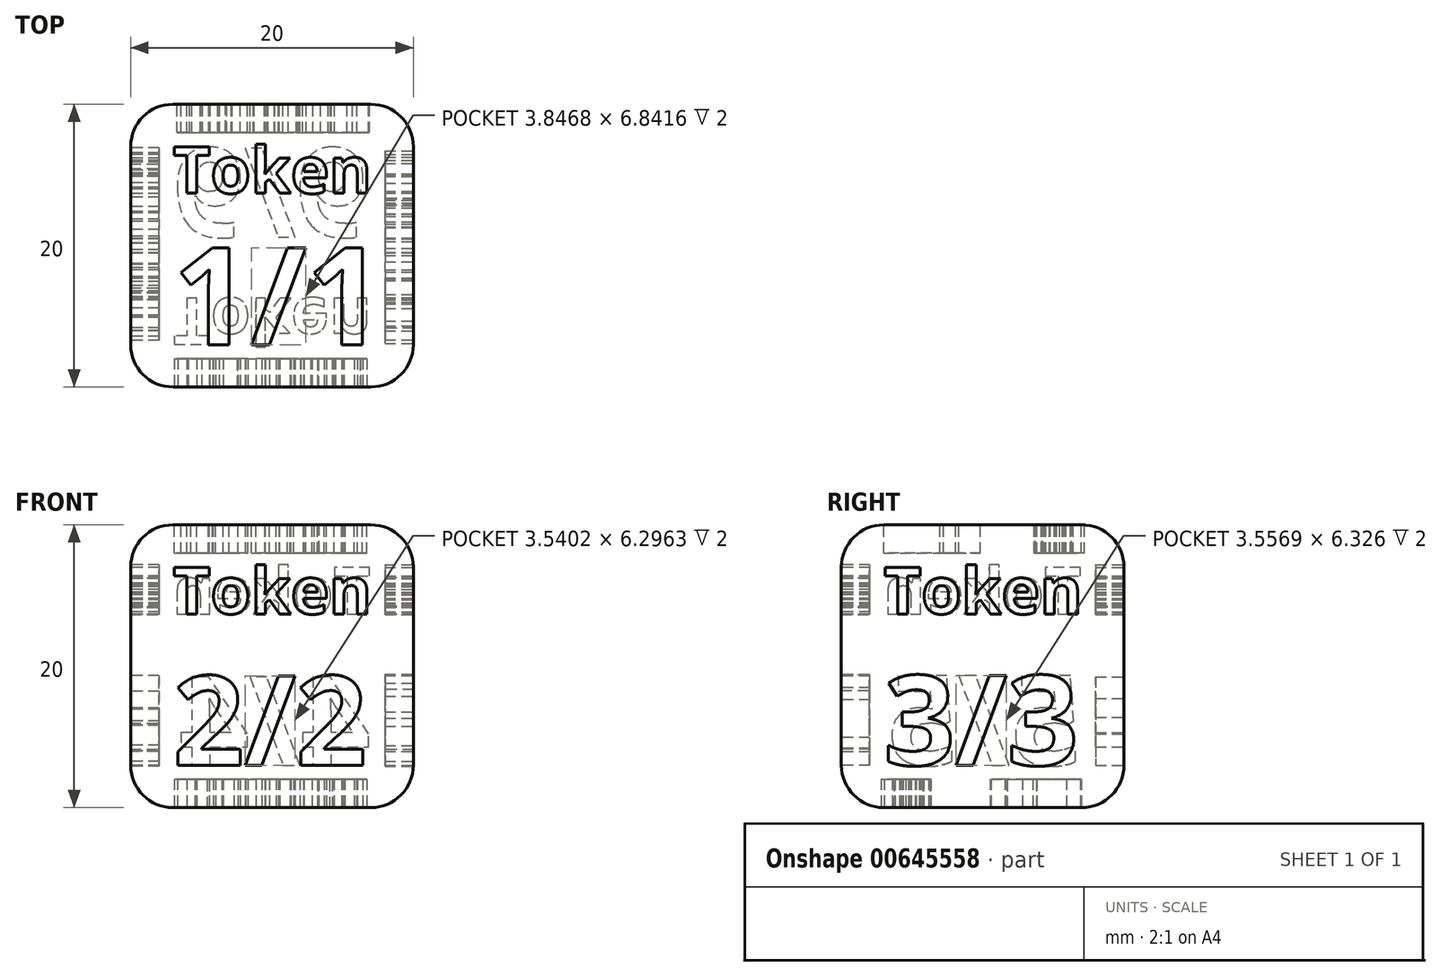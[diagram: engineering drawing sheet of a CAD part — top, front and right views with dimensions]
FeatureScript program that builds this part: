
annotation { "Feature Type Name" : "Feature", "Feature Type Description" : "" }
export const myFeature = defineFeature(function(context is Context, id is Id, definition is map)
    precondition{}
    {
        {
            var Q0;
            Q0=qCreatedBy(makeId("Top.planeOp"),FACE);
            var sketch = newSketch(context, id + "F0", { "sketchPlane" : qUnion([Q0])});
            skLineSegment(sketch, "E0.bottom", {"start": v(0, 0) * mm, "end": v(20, 0) * mm});
            skLineSegment(sketch, "E0.top", {"start": v(0, 20) * mm, "end": v(20, 20) * mm});
            skLineSegment(sketch, "E0.left", {"start": v(0, 0) * mm, "end": v(0, 20) * mm});
            skLineSegment(sketch, "E0.right", {"start": v(20, 0) * mm, "end": v(20, 20) * mm});
            skSolve(sketch);
        }
        {
            var Q0;
            Q0 = qSketchRegion(id + "F0", true);
            extrude(context, id + "F1", {"entities" : qUnion([Q0]), "depth" : 20 * mm, "offsetDistance" : 25 * mm});
        }
        {
            var Q0;
            Q0=makeQuery(id+"F1.opExtrude","CAP_EDGE",EDGE,{"disambiguationData":[OSD([sQuery(id+"F0.wireOp",EDGE,"E0.top")])],"isStart":true});
            var Q1;
            Q1=makeQuery(id+"F1.opExtrude","CAP_EDGE",EDGE,{"disambiguationData":[OSD([sQuery(id+"F0.wireOp",EDGE,"E0.left")])],"isStart":true});
            var Q2;
            Q2=makeQuery(id+"F1.opExtrude","SWEPT_EDGE",EDGE,{"disambiguationData":[OSD([sQuery(id+"F0.wireOp",EDGE,"E0.top"),sQuery(id+"F0.wireOp",EDGE,"E0.left")])]});
            var Q3;
            Q3=makeQuery(id+"F1.opExtrude","SWEPT_EDGE",EDGE,{"disambiguationData":[OSD([sQuery(id+"F0.wireOp",EDGE,"E0.top"),sQuery(id+"F0.wireOp",EDGE,"E0.right")])]});
            var Q4;
            Q4=makeQuery(id+"F1.opExtrude","CAP_EDGE",EDGE,{"disambiguationData":[OSD([sQuery(id+"F0.wireOp",EDGE,"E0.top")])],"isStart":false});
            var Q5;
            Q5=makeQuery(id+"F1.opExtrude","CAP_EDGE",EDGE,{"disambiguationData":[OSD([sQuery(id+"F0.wireOp",EDGE,"E0.right")])],"isStart":false});
            var Q6;
            Q6=makeQuery(id+"F1.opExtrude","CAP_EDGE",EDGE,{"disambiguationData":[OSD([sQuery(id+"F0.wireOp",EDGE,"E0.left")])],"isStart":false});
            var Q7;
            Q7=makeQuery(id+"F1.opExtrude","SWEPT_EDGE",EDGE,{"disambiguationData":[OSD([sQuery(id+"F0.wireOp",EDGE,"E0.bottom"),sQuery(id+"F0.wireOp",EDGE,"E0.left")])]});
            var Q8;
            Q8=makeQuery(id+"F1.opExtrude","CAP_EDGE",EDGE,{"disambiguationData":[OSD([sQuery(id+"F0.wireOp",EDGE,"E0.bottom")])],"isStart":false});
            var Q9;
            Q9=makeQuery(id+"F1.opExtrude","SWEPT_EDGE",EDGE,{"disambiguationData":[OSD([sQuery(id+"F0.wireOp",EDGE,"E0.bottom"),sQuery(id+"F0.wireOp",EDGE,"E0.right")])]});
            var Q10;
            Q10=makeQuery(id+"F1.opExtrude","CAP_EDGE",EDGE,{"disambiguationData":[OSD([sQuery(id+"F0.wireOp",EDGE,"E0.right")])],"isStart":true});
            var Q11;
            Q11=makeQuery(id+"F1.opExtrude","CAP_EDGE",EDGE,{"disambiguationData":[OSD([sQuery(id+"F0.wireOp",EDGE,"E0.bottom")])],"isStart":true});
            fillet(context, id + "F2", {"entities" : qUnion([Q0, Q1, Q2, Q3, Q4, Q5, Q6, Q7, Q8, Q9, Q10, Q11]), "radius" : 3 * mm, "tangentPropagation" : true, "allowEdgeOverflow" : false});
        }
        {
            var Q0;
            Q0=makeQuery(id+"F1.opExtrude","CAP_FACE",FACE,{"disambiguationData":[OSD([sQuery(id+"F0.wireOp",EDGE,"E0.bottom"),sQuery(id+"F0.wireOp",EDGE,"E0.top"),sQuery(id+"F0.wireOp",EDGE,"E0.left"),sQuery(id+"F0.wireOp",EDGE,"E0.right")])],"isStart":false});
            var sketch = newSketch(context, id + "F3", { "sketchPlane" : qUnion([Q0])});
            skText(sketch, "E1", { "text": "Token", "fontName": "OpenSans-Bold.ttf"});
            skText(sketch, "E2", { "text": "1/1", "fontName": "OpenSans-Bold.ttf"});
            const initialGuessF3  = {"E1": [0.003, 0.0137, 1, 0, 0.0033], "E2": [0.003, 0.003, 1, 0, 0.0069]};
            skSetInitialGuess(sketch, initialGuessF3);
            skSolve(sketch);
        }
        {
            var Q0;
            Q0=makeQuery(id+"F1.opExtrude","SWEPT_FACE",FACE,{"disambiguationData":[OSD([sQuery(id+"F0.wireOp",EDGE,"E0.bottom")])]});
            var sketch = newSketch(context, id + "F4", { "sketchPlane" : qUnion([Q0])});
            skText(sketch, "E3", { "text": "Token", "fontName": "OpenSans-Bold.ttf"});
            skText(sketch, "E4", { "text": "2/2", "fontName": "OpenSans-Bold.ttf"});
            const initialGuessF4  = {"E3": [0.003, 0.0137, 1, 0, 0.0033], "E4": [0.003, 0.003, 1, 0, 0.00635]};
            skSetInitialGuess(sketch, initialGuessF4);
            skSolve(sketch);
        }
        {
            var Q0;
            Q0=makeQuery(id+"F1.opExtrude","SWEPT_FACE",FACE,{"disambiguationData":[OSD([sQuery(id+"F0.wireOp",EDGE,"E0.right")])]});
            var sketch = newSketch(context, id + "F5", { "sketchPlane" : qUnion([Q0])});
            skText(sketch, "E5", { "text": "Token", "fontName": "OpenSans-Bold.ttf"});
            skText(sketch, "E6", { "text": "3/3", "fontName": "OpenSans-Bold.ttf"});
            const initialGuessF5  = {"E5": [0.003, 0.0137, 1, 0, 0.0033], "E6": [0.003, 0.003, 1, 0, 0.00638]};
            skSetInitialGuess(sketch, initialGuessF5);
            skSolve(sketch);
        }
        {
            var Q0;
            Q0=makeQuery(id+"F1.opExtrude","SWEPT_FACE",FACE,{"disambiguationData":[OSD([sQuery(id+"F0.wireOp",EDGE,"E0.top")])]});
            var sketch = newSketch(context, id + "F6", { "sketchPlane" : qUnion([Q0])});
            skText(sketch, "E7", { "text": "Token", "fontName": "OpenSans-Bold.ttf"});
            skText(sketch, "E8", { "text": "4/4", "fontName": "OpenSans-Bold.ttf"});
            const initialGuessF6  = {"E7": [-0.017, 0.0137, 1, 0, 0.0033], "E8": [-0.017, 0.003, 1, 0, 0.00628]};
            skSetInitialGuess(sketch, initialGuessF6);
            skSolve(sketch);
        }
        {
            var Q0;
            Q0=makeQuery(id+"F1.opExtrude","SWEPT_FACE",FACE,{"disambiguationData":[OSD([sQuery(id+"F0.wireOp",EDGE,"E0.left")])]});
            var sketch = newSketch(context, id + "F7", { "sketchPlane" : qUnion([Q0])});
            skText(sketch, "E9", { "text": "Token", "fontName": "OpenSans-Bold.ttf"});
            skText(sketch, "E10", { "text": "5/5", "fontName": "OpenSans-Bold.ttf"});
            const initialGuessF7  = {"E9": [-0.017, 0.0137, 1, 0, 0.0033], "E10": [-0.017, 0.003, 1, 0, 0.0064]};
            skSetInitialGuess(sketch, initialGuessF7);
            skSolve(sketch);
        }
        {
            var Q0;
            Q0=makeQuery(id+"F1.opExtrude","CAP_FACE",FACE,{"disambiguationData":[OSD([sQuery(id+"F0.wireOp",EDGE,"E0.bottom"),sQuery(id+"F0.wireOp",EDGE,"E0.top"),sQuery(id+"F0.wireOp",EDGE,"E0.left"),sQuery(id+"F0.wireOp",EDGE,"E0.right")])],"isStart":true});
            var sketch = newSketch(context, id + "F8", { "sketchPlane" : qUnion([Q0])});
            skText(sketch, "E11", { "text": "Token", "fontName": "OpenSans-Bold.ttf"});
            skText(sketch, "E12", { "text": "6/6", "fontName": "OpenSans-Bold.ttf"});
            const initialGuessF8  = {"E11": [0.003, -0.0063, 1, 0, 0.0033], "E12": [0.003, -0.0169, 1, 0, 0.00635]};
            skSetInitialGuess(sketch, initialGuessF8);
            skSolve(sketch);
        }
        {
            var Q0;
            Q0 = qSketchRegion(id + "F3", true);
            extrude(context, id + "F9", {"entities" : qUnion([Q0]), "operationType" : NewBodyOperationType.REMOVE, "oppositeDirection" : true, "depth" : 2 * mm, "offsetDistance" : 25 * mm});
        }
        {
            var Q0;
            Q0 = qSketchRegion(id + "F4", true);
            extrude(context, id + "F10", {"entities" : qUnion([Q0]), "operationType" : NewBodyOperationType.REMOVE, "oppositeDirection" : true, "depth" : 2 * mm, "offsetDistance" : 25 * mm});
        }
        {
            var Q0;
            Q0 = qSketchRegion(id + "F5", true);
            extrude(context, id + "F11", {"entities" : qUnion([Q0]), "operationType" : NewBodyOperationType.REMOVE, "oppositeDirection" : true, "depth" : 2 * mm, "offsetDistance" : 25 * mm});
        }
        {
            var Q0;
            Q0 = qSketchRegion(id + "F6", true);
            extrude(context, id + "F12", {"entities" : qUnion([Q0]), "operationType" : NewBodyOperationType.REMOVE, "oppositeDirection" : true, "depth" : 2 * mm, "offsetDistance" : 25 * mm});
        }
        {
            var Q0;
            Q0 = qSketchRegion(id + "F7", true);
            extrude(context, id + "F13", {"entities" : qUnion([Q0]), "operationType" : NewBodyOperationType.REMOVE, "oppositeDirection" : true, "depth" : 2 * mm, "offsetDistance" : 25 * mm});
        }
        {
            var Q0;
            Q0 = qSketchRegion(id + "F8", true);
            extrude(context, id + "F14", {"entities" : qUnion([Q0]), "operationType" : NewBodyOperationType.REMOVE, "oppositeDirection" : true, "depth" : 2 * mm, "offsetDistance" : 25 * mm});
        }
    });
